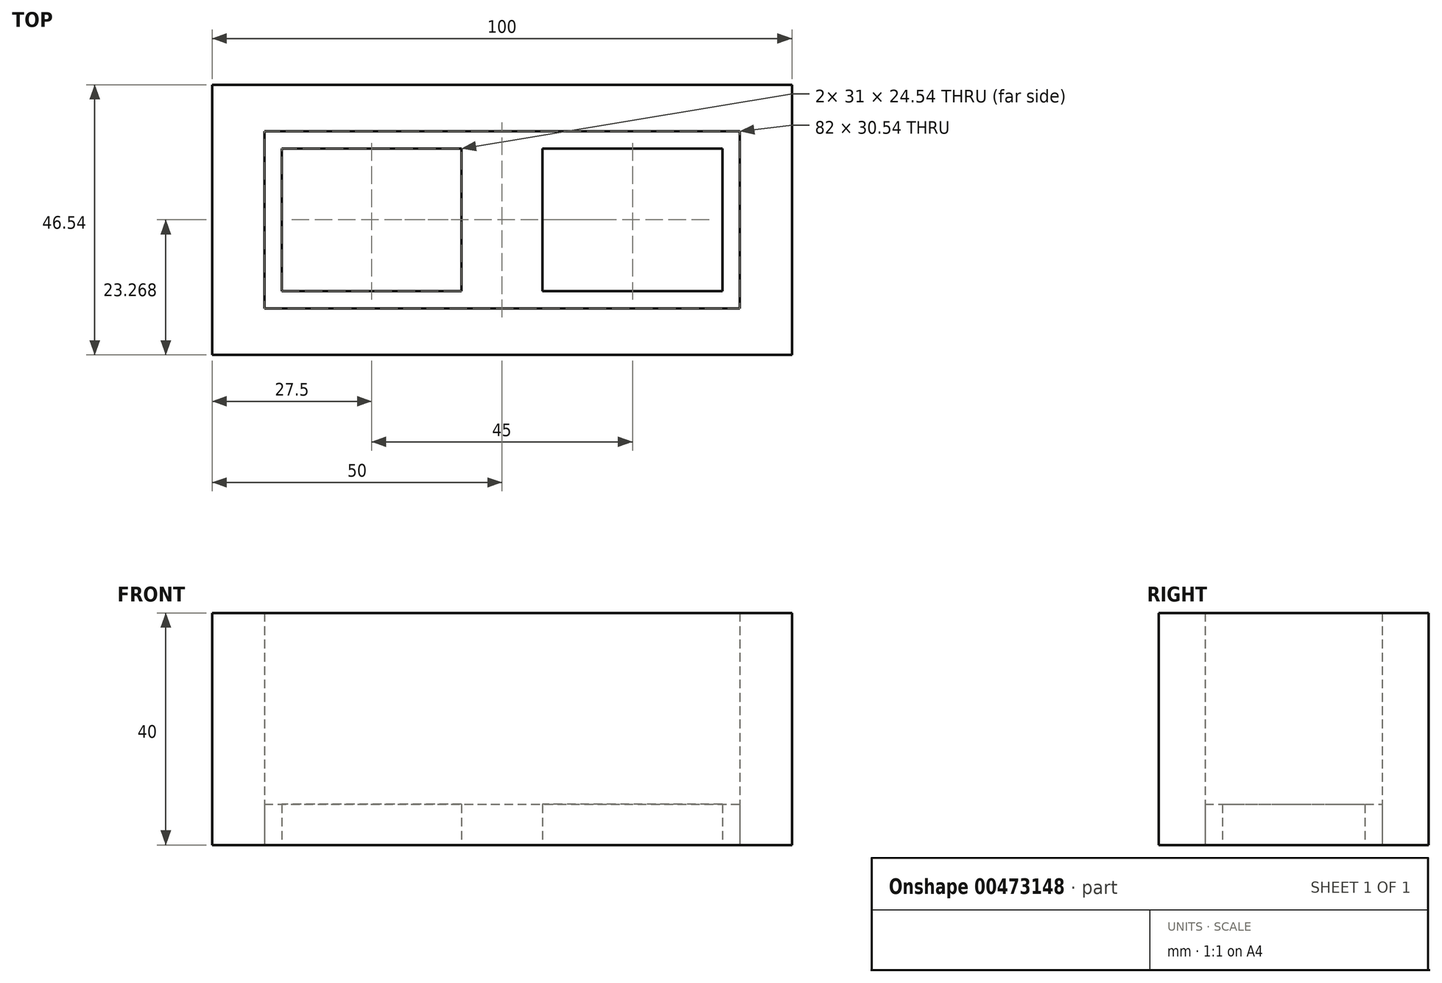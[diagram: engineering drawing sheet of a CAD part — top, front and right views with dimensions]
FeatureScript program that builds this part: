
annotation { "Feature Type Name" : "Feature", "Feature Type Description" : "" }
export const myFeature = defineFeature(function(context is Context, id is Id, definition is map)
    precondition{}
    {
        {
            var Q0;
            Q0=qCreatedBy(makeId("Top.planeOp"),FACE);
            var sketch = newSketch(context, id + "F0", { "sketchPlane" : qUnion([Q0])});
            skLineSegment(sketch, "E0", {"start": v(-50, 23.06) * mm, "end": v(0, 23.06) * mm});
            skLineSegment(sketch, "E1", {"start": v(0, 23.06) * mm, "end": v(50, 23.06) * mm});
            skLineSegment(sketch, "E2", {"start": v(50, 23.06) * mm, "end": v(50, 0) * mm});
            skLineSegment(sketch, "E3", {"start": v(50, 0) * mm, "end": v(50, -23.48) * mm});
            skLineSegment(sketch, "E4", {"start": v(50, -23.48) * mm, "end": v(-50, -23.48) * mm});
            skLineSegment(sketch, "E5", {"start": v(-50, -23.48) * mm, "end": v(-50, 23.06) * mm});
            skLineSegment(sketch, "E6", {"start": v(-38, -12.48) * mm, "end": v(-38, 12.06) * mm});
            skLineSegment(sketch, "E7", {"start": v(-38, 12.06) * mm, "end": v(-7, 12.06) * mm});
            skLineSegment(sketch, "E8", {"start": v(-7, 12.06) * mm, "end": v(-7, -12.48) * mm});
            skLineSegment(sketch, "E9", {"start": v(-7, -12.48) * mm, "end": v(-38, -12.48) * mm});
            skLineSegment(sketch, "E10", {"start": v(7, -12.48) * mm, "end": v(7, 12.06) * mm});
            skLineSegment(sketch, "E11", {"start": v(7, 12.06) * mm, "end": v(38, 12.06) * mm});
            skLineSegment(sketch, "E12", {"start": v(38, 12.06) * mm, "end": v(38, -12.48) * mm});
            skLineSegment(sketch, "E13", {"start": v(38, -12.48) * mm, "end": v(7, -12.48) * mm});
            skLineSegment(sketch, "E14", {"start": v(-41, -15.48) * mm, "end": v(-41, 15.06) * mm});
            skLineSegment(sketch, "E15", {"start": v(-41, 15.06) * mm, "end": v(41, 15.06) * mm});
            skLineSegment(sketch, "E16", {"start": v(41, 15.06) * mm, "end": v(41, -15.48) * mm});
            skLineSegment(sketch, "E17", {"start": v(-41, -15.48) * mm, "end": v(41, -15.48) * mm});
            skSolve(sketch);
        }
        {
            var Q0;
            Q0=makeQuery(id+"F0.imprint","IMPRINT",FACE,{"disambiguationData":[TD([[makeQuery(id+"F0.imprint","IMPRINT",EDGE,{"derivedFrom":sQuery(id+"F0.wireOp",EDGE,"E0")}),-1.0]])]});
            extrude(context, id + "F1", {"entities" : qUnion([Q0]), "depth" : 40 * mm});
        }
        {
            var Q0;
            Q0=makeQuery(id+"F0.imprint","IMPRINT",FACE,{"disambiguationData":[TD([[makeQuery(id+"F0.imprint","IMPRINT",EDGE,{"derivedFrom":sQuery(id+"F0.wireOp",EDGE,"E6")}),1.0]])]});
            var Q1;
            Q1=sQuery(id+"F0.wireOp",EDGE,"E15");
            var Q2;
            Q2=sQuery(id+"F0.wireOp",EDGE,"E17");
            var Q3;
            Q3=sQuery(id+"F0.wireOp",EDGE,"E14");
            var Q4;
            Q4=sQuery(id+"F0.wireOp",EDGE,"E16");
            var Q5;
            Q5=sQuery(id+"F0.wireOp",EDGE,"E12");
            var Q6;
            Q6=sQuery(id+"F0.wireOp",EDGE,"E13");
            var Q7;
            Q7=sQuery(id+"F0.wireOp",EDGE,"E10");
            var Q8;
            Q8=sQuery(id+"F0.wireOp",EDGE,"E11");
            var Q9;
            Q9=sQuery(id+"F0.wireOp",EDGE,"E7");
            var Q10;
            Q10=sQuery(id+"F0.wireOp",EDGE,"E8");
            var Q11;
            Q11=sQuery(id+"F0.wireOp",EDGE,"E9");
            var Q12;
            Q12=sQuery(id+"F0.wireOp",EDGE,"E6");
            extrude(context, id + "F2", {"entities" : qUnion([Q0]), "surfaceEntities" : qUnion([Q1, Q2, Q3, Q4, Q5, Q6, Q7, Q8, Q9, Q10, Q11, Q12]), "depth" : 7 * mm});
        }
    });
